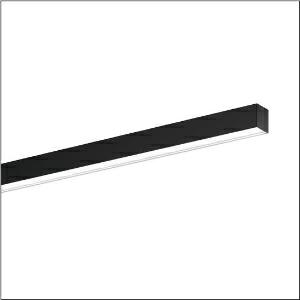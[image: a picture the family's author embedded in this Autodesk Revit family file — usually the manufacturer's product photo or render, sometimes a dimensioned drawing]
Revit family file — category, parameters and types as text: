
# Revit family: silica_r__21_51mx23da44bb_c0fe
name_source: partatom
category: Lighting Fixtures
units: mm (PartAtom-declared; Revit-internal decimal feet)

## family parameters
Cut with Voids When Loaded = No
Host = Face
Light Source = No
Part Type = Normal
Room Calculation Point = No
Round Connector Dimension = Use Diameter
Shared = No

## types (1)
- --- (1 x LED, 3280 lm, 22.4 W, 4000K)
    Apparent Load = 22 VA
    CIE Flux Codes = 78 96 99 100 100
    Color Rendering = 80
    Color Temperature = 4000K
    Default Elevation = 1800 mm
    Description = Silica® 21, office luminaire, primary optical cover: prismatic diffuser, of PMMA, CAT 2 (L<= 3000cd/m²), light emission: direct distribution, primary light characteristic: symmetric, installation type: surface-mounted, LED, rated luminous flux: 3.280lm, luminous efficacy: 146lm/W, light colour: 840, colour temperature: 4000K, with terminal, 3+2-pole, max. 2.5mm², mains connection: 220..240V, AC, 50/60Hz, rated input power: 22.4W, luminaire housing, of aluminium, jet black (RAL 9005), length: 1.204mm, width: 53mm, height: 53mm, protection rating (complete): IP20, insulation class (complete): insulation class I (protective earthing), certification: CE, permissible operating ambient temperature: 0..+35°C, standard: EN 50419, packaging unit: 1 piece
    Height = 0 mm  [stored 0 ft]
    Lamp = 1 x LED
    Lamp Light Flux = 3280 lm
    Lamp Power = 22.4 W
    Lamp count = 1
    Length = 1204 mm
    Luminous efficacy = 146 lm/W
    Manufacturer = Siteco
    ModVariant = No
    Model = 51MX23DA44BB
    Mounting Place = Ceiling
    Mounting Type = Recessed
    Number of Poles = 1
    OnlyDefault = Yes
    Power Factor = 1
    Product Name = Silica® 21
    Product group = office luminaire | ceiling recessed
    ProductGroupID = 401
    Protection Class = Protection class I
    Protection Degree = IP 20
    RLX_Detail_Level = 1
    RLX_Emergency_Light_Flux = 0 lm
    RLX_Emergency_Type = 0
    RLX_Emergency_Type_DB = No
    RlxData = <blob elided: 23685 chars, md5=c96fe7c9>
    Socket = socket
    Standby Power = 0 W
    System Light Flux = 3280 lm
    System Power = 22 W
    Type Comments = factory setting: luminous flux: 100 % | dim-lin: 254 | 323 mA
    Type Image = l_1313584.jpg
    URL = http://relux.com
    VarID = @adj_068191
    Voltage = 0 V
    Weight = 0.00 kg
    Width = 53 mm

note: [stored X ft] marks values corroborated as IEEE doubles in the binary element streams (Revit-internal decimal feet)

## geometry (parser evidence)
native form markers: Blend x4, Sweep x14
no freeform markers — native parametric forms only
